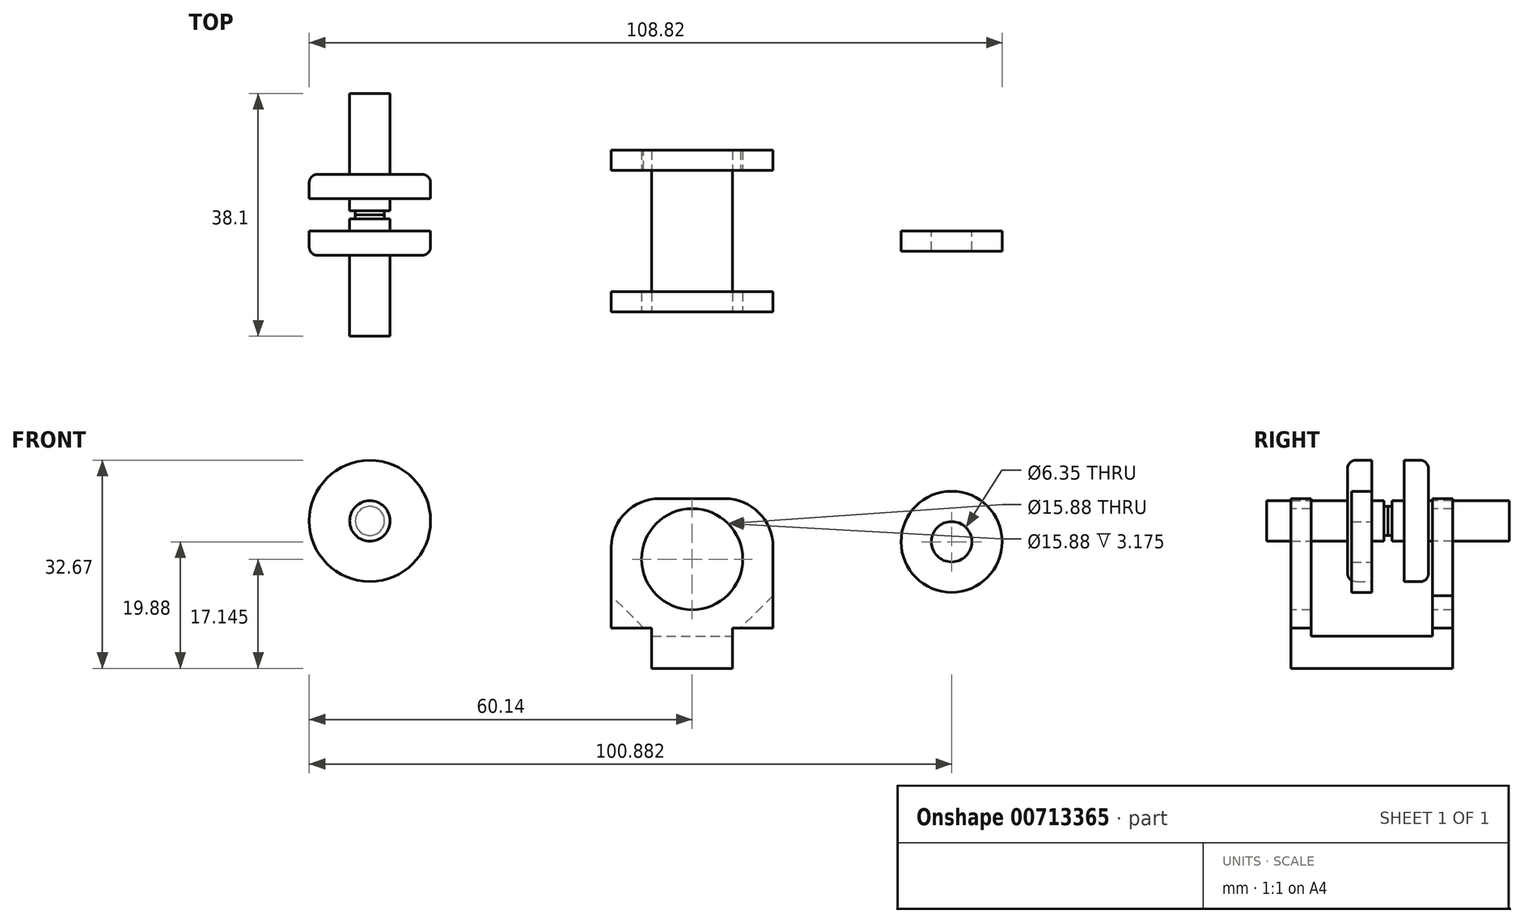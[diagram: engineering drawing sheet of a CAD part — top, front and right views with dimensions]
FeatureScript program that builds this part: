
annotation { "Feature Type Name" : "Feature", "Feature Type Description" : "" }
export const myFeature = defineFeature(function(context is Context, id is Id, definition is map)
    precondition{}
    {
        {
            var Q0;
            Q0=qCreatedBy(makeId("Top.planeOp"),FACE);
            var sketch = newSketch(context, id + "F0", { "sketchPlane" : qUnion([Q0])});
            skLineSegment(sketch, "E0.bottom", {"start": v(12.7, 12.7) * mm, "end": v(-12.7, 12.7) * mm});
            skLineSegment(sketch, "E0.top", {"start": v(12.7, -12.7) * mm, "end": v(-12.7, -12.7) * mm});
            skLineSegment(sketch, "E0.left", {"start": v(12.7, 12.7) * mm, "end": v(12.7, -12.7) * mm});
            skLineSegment(sketch, "E0.right", {"start": v(-12.7, 12.7) * mm, "end": v(-12.7, -12.7) * mm});
            skPoint(sketch, "E0.middle", {"position": v(0, 0) * mm});
            skSolve(sketch);
        }
        {
            var Q0;
            Q0 = qSketchRegion(id + "F0", true);
            extrude(context, id + "F1", {"entities" : qUnion([Q0]), "depth" : 26.67 * mm, "offsetDistance" : 25.4 * mm});
        }
        {
            var Q0;
            Q0=makeQuery(id+"F1.opExtrude","CAP_FACE",FACE,{"disambiguationData":[OSD([sQuery(id+"F0.wireOp",EDGE,"E0.bottom"),sQuery(id+"F0.wireOp",EDGE,"E0.top"),sQuery(id+"F0.wireOp",EDGE,"E0.left"),sQuery(id+"F0.wireOp",EDGE,"E0.right")])],"isStart":false});
            var sketch = newSketch(context, id + "F2", { "sketchPlane" : qUnion([Q0])});
            skLineSegment(sketch, "E1.bottom", {"start": v(-12.7, 9.53) * mm, "end": v(12.7, 9.53) * mm});
            skLineSegment(sketch, "E1.top", {"start": v(-12.7, -9.53) * mm, "end": v(12.7, -9.53) * mm});
            skLineSegment(sketch, "E1.left", {"start": v(-12.7, 9.53) * mm, "end": v(-12.7, -9.53) * mm});
            skLineSegment(sketch, "E1.right", {"start": v(12.7, 9.53) * mm, "end": v(12.7, -9.53) * mm});
            skPoint(sketch, "E1.middle", {"position": v(0, 0) * mm});
            skSolve(sketch);
        }
        {
            var Q0;
            Q0 = qSketchRegion(id + "F2", true);
            extrude(context, id + "F3", {"entities" : qUnion([Q0]), "operationType" : NewBodyOperationType.REMOVE, "oppositeDirection" : true, "depth" : 21.59 * mm, "offsetDistance" : 25.4 * mm});
        }
        {
            var Q0;
            Q0=makeQuery(id+"F1.opExtrude","SWEPT_FACE",FACE,{"disambiguationData":[OSD([sQuery(id+"F0.wireOp",EDGE,"E0.top")])]});
            var sketch = newSketch(context, id + "F4", { "sketchPlane" : qUnion([Q0])});
            skCircle(sketch, "E2", {"center": v(0, 17.14) * mm, "radius": 7.94 * mm});
            skLineSegment(sketch, "E3.bottom", {"start": v(-12.7, 0) * mm, "end": v(-6.35, 0) * mm});
            skLineSegment(sketch, "E3.top", {"start": v(-12.7, 6.35) * mm, "end": v(-6.35, 6.35) * mm});
            skLineSegment(sketch, "E3.left", {"start": v(-12.7, 0) * mm, "end": v(-12.7, 6.35) * mm});
            skLineSegment(sketch, "E3.right", {"start": v(-6.35, 0) * mm, "end": v(-6.35, 6.35) * mm});
            skLineSegment(sketch, "E4.bottom", {"start": v(12.7, 0) * mm, "end": v(6.35, 0) * mm});
            skLineSegment(sketch, "E4.top", {"start": v(12.7, 6.35) * mm, "end": v(6.35, 6.35) * mm});
            skLineSegment(sketch, "E4.left", {"start": v(12.7, 0) * mm, "end": v(12.7, 6.35) * mm});
            skLineSegment(sketch, "E4.right", {"start": v(6.35, 0) * mm, "end": v(6.35, 6.35) * mm});
            skSolve(sketch);
        }
        {
            var Q0;
            Q0 = qSketchRegion(id + "F4", true);
            extrude(context, id + "F5", {"entities" : qUnion([Q0]), "operationType" : NewBodyOperationType.REMOVE, "oppositeDirection" : true, "depth" : 25.4 * mm, "offsetDistance" : 25.4 * mm});
        }
        {
            var Q0;
            {var subQ0=sQuery(id+"F0.wireOp",EDGE,"E0.left");var subQ1=sQuery(id+"F0.wireOp",EDGE,"E0.top");Q0=makeQuery(id+"F3.boolean.opBoolean","SPLIT",EDGE,{"disambiguationData":[TD([makeQuery(id+"F1.opExtrude","SWEPT_FACE",FACE,{"disambiguationData":[OSD([subQ1])]})])],"derivedFrom":makeQuery(id+"F1.opExtrude","CAP_EDGE",EDGE,{"disambiguationData":[OSD([subQ0])],"isStart":false})});}
            var Q1;
            {var subQ0=sQuery(id+"F0.wireOp",EDGE,"E0.right");var subQ1=sQuery(id+"F0.wireOp",EDGE,"E0.top");Q1=makeQuery(id+"F3.boolean.opBoolean","SPLIT",EDGE,{"disambiguationData":[TD([makeQuery(id+"F1.opExtrude","SWEPT_FACE",FACE,{"disambiguationData":[OSD([subQ1])]})])],"derivedFrom":makeQuery(id+"F1.opExtrude","CAP_EDGE",EDGE,{"disambiguationData":[OSD([subQ0])],"isStart":false})});}
            var Q2;
            {var subQ0=sQuery(id+"F0.wireOp",EDGE,"E0.bottom");var subQ1=sQuery(id+"F0.wireOp",EDGE,"E0.left");Q2=makeQuery(id+"F3.boolean.opBoolean","SPLIT",EDGE,{"disambiguationData":[TD([makeQuery(id+"F1.opExtrude","SWEPT_FACE",FACE,{"disambiguationData":[OSD([subQ0])]})])],"derivedFrom":makeQuery(id+"F1.opExtrude","CAP_EDGE",EDGE,{"disambiguationData":[OSD([subQ1])],"isStart":false})});}
            var Q3;
            {var subQ0=sQuery(id+"F0.wireOp",EDGE,"E0.bottom");var subQ1=sQuery(id+"F0.wireOp",EDGE,"E0.right");Q3=makeQuery(id+"F3.boolean.opBoolean","SPLIT",EDGE,{"disambiguationData":[TD([makeQuery(id+"F1.opExtrude","SWEPT_FACE",FACE,{"disambiguationData":[OSD([subQ0])]})])],"derivedFrom":makeQuery(id+"F1.opExtrude","CAP_EDGE",EDGE,{"disambiguationData":[OSD([subQ1])],"isStart":false})});}
            fillet(context, id + "F6", {"entities" : qUnion([Q0, Q1, Q2, Q3]), "radius" : 7.62 * mm, "tangentPropagation" : true, "allowEdgeOverflow" : false});
        }
        {
            var Q0;
            Q0=qCreatedBy(makeId("Front.planeOp"),FACE);
            var sketch = newSketch(context, id + "F7", { "sketchPlane" : qUnion([Q0])});
            skCircle(sketch, "E5", {"center": v(-50.61, 23.15) * mm, "radius": 9.53 * mm});
            skCircle(sketch, "E6", {"center": v(-50.61, 23.15) * mm, "radius": 3.18 * mm});
            skSolve(sketch);
        }
        {
            var Q0;
            Q0 = qSketchRegion(id + "F7", true);
            extrude(context, id + "F8", {"entities" : qUnion([Q0]), "depth" : 3.8 * mm, "offsetDistance" : 25.4 * mm});
        }
        {
            var Q0;
            Q0=makeQuery(id+"F8.opExtrude","CAP_EDGE",EDGE,{"disambiguationData":[OSD([sQuery(id+"F7.wireOp",EDGE,"E5")])],"isStart":false});
            fillet(context, id + "F9", {"entities" : qUnion([Q0]), "radius" : 1.27 * mm, "tangentPropagation" : true, "allowEdgeOverflow" : false});
        }
        {
            var Q0;
            Q0=makeQuery(id+"F7.imprint","IMPRINT",FACE,{"disambiguationData":[TD([[makeQuery(id+"F7.imprint","IMPRINT",EDGE,{"derivedFrom":sQuery(id+"F7.wireOp",EDGE,"E6")}),1.0]])]});
            extrude(context, id + "F10", {"entities" : qUnion([Q0]), "operationType" : NewBodyOperationType.ADD, "depth" : 16.5 * mm, "offsetDistance" : 25.4 * mm});
        }
        {
            var Q0;
            Q0=makeQuery(id+"F7.imprint","IMPRINT",FACE,{"disambiguationData":[TD([[makeQuery(id+"F7.imprint","IMPRINT",EDGE,{"derivedFrom":sQuery(id+"F7.wireOp",EDGE,"E6")}),1.0]])]});
            extrude(context, id + "F11", {"entities" : qUnion([Q0]), "operationType" : NewBodyOperationType.ADD, "oppositeDirection" : true, "depth" : 2.54 * mm, "offsetDistance" : 25.4 * mm});
        }
        {
            var Q0;
            Q0=makeQuery(id+"F11.opExtrude","CAP_FACE",FACE,{"disambiguationData":[OSD([sQuery(id+"F7.wireOp",EDGE,"E6")])],"isStart":false});
            var sketch = newSketch(context, id + "F12", { "sketchPlane" : qUnion([Q0])});
            skCircle(sketch, "E7", {"center": v(50.61, 23.15) * mm, "radius": 2.29 * mm});
            skCircle(sketch, "E8", {"center": v(50.61, 23.15) * mm, "radius": 3.18 * mm});
            skSolve(sketch);
        }
        {
            var Q0;
            Q0=makeQuery(id+"F12.imprint","IMPRINT",FACE,{"disambiguationData":[TD([[makeQuery(id+"F12.imprint","IMPRINT",EDGE,{"derivedFrom":sQuery(id+"F12.wireOp",EDGE,"E7")}),-1.0]])]});
            extrude(context, id + "F13", {"entities" : qUnion([Q0]), "operationType" : NewBodyOperationType.REMOVE, "endBound" : BoundingType.SYMMETRIC, "oppositeDirection" : true, "depth" : 1.28 * mm, "offsetDistance" : 25.4 * mm});
        }
        {
            var Q0;
            Q0=makeQuery(id+"F8.opExtrude","SWEPT_BODY",BODY,{"disambiguationData":[OSD([sQuery(id+"F7.wireOp",EDGE,"E5"),sQuery(id+"F7.wireOp",EDGE,"E6")])]});
            var Q1;
            Q1=makeQuery(id+"F11.opExtrude","CAP_FACE",FACE,{"disambiguationData":[OSD([sQuery(id+"F7.wireOp",EDGE,"E6")])],"isStart":false});
            mirror(context, id + "F14", {"operationType" : NewBodyOperationType.ADD, "entities" : qUnion([Q0]), "mirrorPlane" : qUnion([Q1])});
        }
        {
            var Q0;
            {var subQ0=sQuery(id+"F0.wireOp",EDGE,"E0.top");var subQ1=sQuery(id+"F0.wireOp",EDGE,"E0.left");var subQ2=sQuery(id+"F4.wireOp",EDGE,"E4.top");Q0=makeQuery(id+"F5.boolean.opBoolean","COPY",EDGE,{"disambiguationData":[TD([makeQuery(id+"F1.opExtrude","SWEPT_FACE",FACE,{"disambiguationData":[OSD([subQ0])]})])],"derivedFrom":makeQuery(id+"F5.opExtrude","SWEPT_EDGE",EDGE,{"disambiguationData":[OSD([subQ0,subQ1,subQ2,sQuery(id+"F4.wireOp",EDGE,"E4.left")])]})});}
            var Q1;
            {var subQ0=sQuery(id+"F0.wireOp",EDGE,"E0.top");var subQ1=sQuery(id+"F0.wireOp",EDGE,"E0.right");var subQ2=sQuery(id+"F4.wireOp",EDGE,"E3.top");Q1=makeQuery(id+"F5.boolean.opBoolean","COPY",EDGE,{"disambiguationData":[TD([makeQuery(id+"F1.opExtrude","SWEPT_FACE",FACE,{"disambiguationData":[OSD([subQ0])]})])],"derivedFrom":makeQuery(id+"F5.opExtrude","SWEPT_EDGE",EDGE,{"disambiguationData":[OSD([subQ0,subQ1,subQ2,sQuery(id+"F4.wireOp",EDGE,"E3.left")])]})});}
            var Q2;
            {var subQ0=sQuery(id+"F0.wireOp",EDGE,"E0.right");var subQ1=sQuery(id+"F4.wireOp",EDGE,"E3.top");Q2=makeQuery(id+"F5.boolean.opBoolean","COPY",EDGE,{"disambiguationData":[TD([makeQuery(id+"F1.opExtrude","SWEPT_FACE",FACE,{"disambiguationData":[OSD([sQuery(id+"F0.wireOp",EDGE,"E0.bottom")])]})])],"derivedFrom":makeQuery(id+"F5.opExtrude","SWEPT_EDGE",EDGE,{"disambiguationData":[OSD([sQuery(id+"F0.wireOp",EDGE,"E0.top"),subQ0,subQ1,sQuery(id+"F4.wireOp",EDGE,"E3.left")])]})});}
            var Q3;
            {var subQ0=sQuery(id+"F4.wireOp",EDGE,"E4.top");var subQ1=sQuery(id+"F0.wireOp",EDGE,"E0.left");Q3=makeQuery(id+"F5.boolean.opBoolean","COPY",EDGE,{"disambiguationData":[TD([makeQuery(id+"F1.opExtrude","SWEPT_FACE",FACE,{"disambiguationData":[OSD([sQuery(id+"F0.wireOp",EDGE,"E0.bottom")])]})])],"derivedFrom":makeQuery(id+"F5.opExtrude","SWEPT_EDGE",EDGE,{"disambiguationData":[OSD([sQuery(id+"F0.wireOp",EDGE,"E0.top"),subQ1,subQ0,sQuery(id+"F4.wireOp",EDGE,"E4.left")])]})});}
            chamfer(context, id + "F15", {"entities" : qUnion([Q0, Q1, Q2, Q3]), "width" : 5.08 * mm, "tangentPropagation" : true});
        }
        {
            var Q0;
            Q0=qCreatedBy(makeId("Front.planeOp"),FACE);
            var sketch = newSketch(context, id + "F16", { "sketchPlane" : qUnion([Q0])});
            skCircle(sketch, "E9", {"center": v(40.74, 19.88) * mm, "radius": 7.94 * mm});
            skCircle(sketch, "E10", {"center": v(40.74, 19.88) * mm, "radius": 3.18 * mm});
            skSolve(sketch);
        }
        {
            var Q0;
            Q0=makeQuery(id+"F16.imprint","IMPRINT",FACE,{"disambiguationData":[TD([[makeQuery(id+"F16.imprint","IMPRINT",EDGE,{"derivedFrom":sQuery(id+"F16.wireOp",EDGE,"E9")}),1.0]])]});
            extrude(context, id + "F17", {"entities" : qUnion([Q0]), "depth" : 3.17 * mm, "offsetDistance" : 25.4 * mm});
        }
    });
